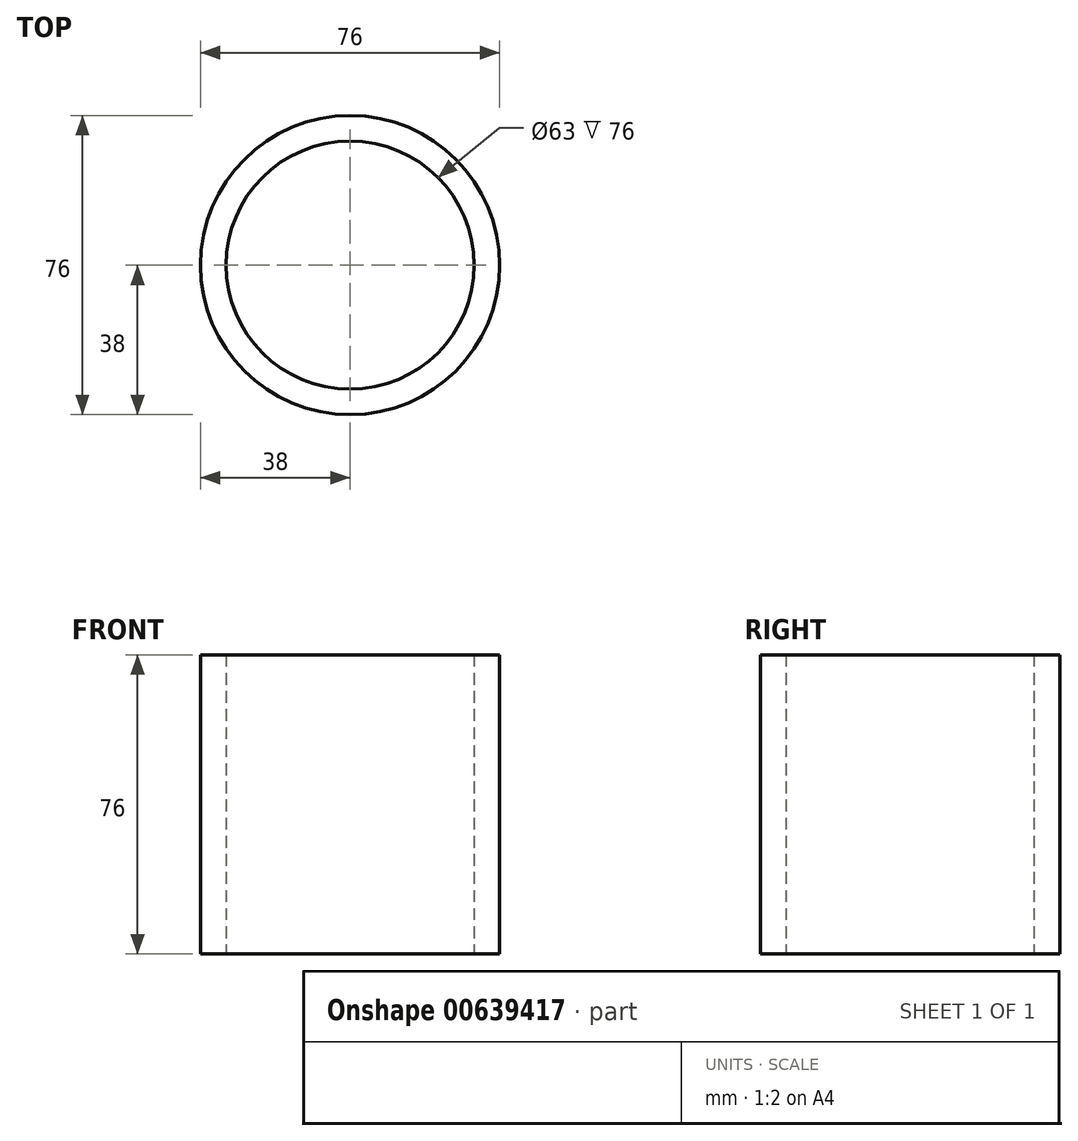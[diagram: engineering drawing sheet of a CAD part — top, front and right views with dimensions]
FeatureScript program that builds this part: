
annotation { "Feature Type Name" : "Feature", "Feature Type Description" : "" }
export const myFeature = defineFeature(function(context is Context, id is Id, definition is map)
    precondition{}
    {
        {
            var Q0;
            Q0=qCreatedBy(makeId("Top.planeOp"),FACE);
            var sketch = newSketch(context, id + "F0", { "sketchPlane" : qUnion([Q0])});
            skCircle(sketch, "E0", {"center": v(0, 0) * mm, "radius": 38 * mm});
            skCircle(sketch, "E1", {"center": v(0, 0) * mm, "radius": 31.5 * mm});
            skSolve(sketch);
        }
        {
            var Q0;
            Q0=makeQuery(id+"F0.imprint","IMPRINT",FACE,{"disambiguationData":[TD([[makeQuery(id+"F0.imprint","IMPRINT",EDGE,{"derivedFrom":sQuery(id+"F0.wireOp",EDGE,"E0")}),1.0]])]});
            extrude(context, id + "F1", {"entities" : qUnion([Q0]), "depth" : 76 * mm, "offsetDistance" : 25 * mm});
        }
    });
